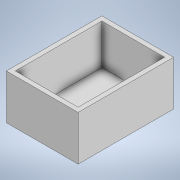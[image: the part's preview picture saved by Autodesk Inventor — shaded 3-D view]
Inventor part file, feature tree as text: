
AUTODESK INVENTOR PART (.ipt)
format: ipt  version: 2022 (Build 260153000, 153)  size: 96,768 bytes
history: native  units: mm
features: extrude x1, shell x1, sketch x1
ambient origin geometry x8: Origin, YZ Plane, XZ Plane, XY Plane, X Axis, Y Axis, Z Axis, Center Point
bodies: Solid1 (feature_tree)
feature tree (3):
  extrude  "Extrusion1"  Depth=160.0mm
  shell  "Shell1"  Thickness=100.0mm
  sketch  "Sketch1"  dims[d0=213.0mm d1=160.0mm d2=100.0mm d3=0.0mm d4=10.0mm]
